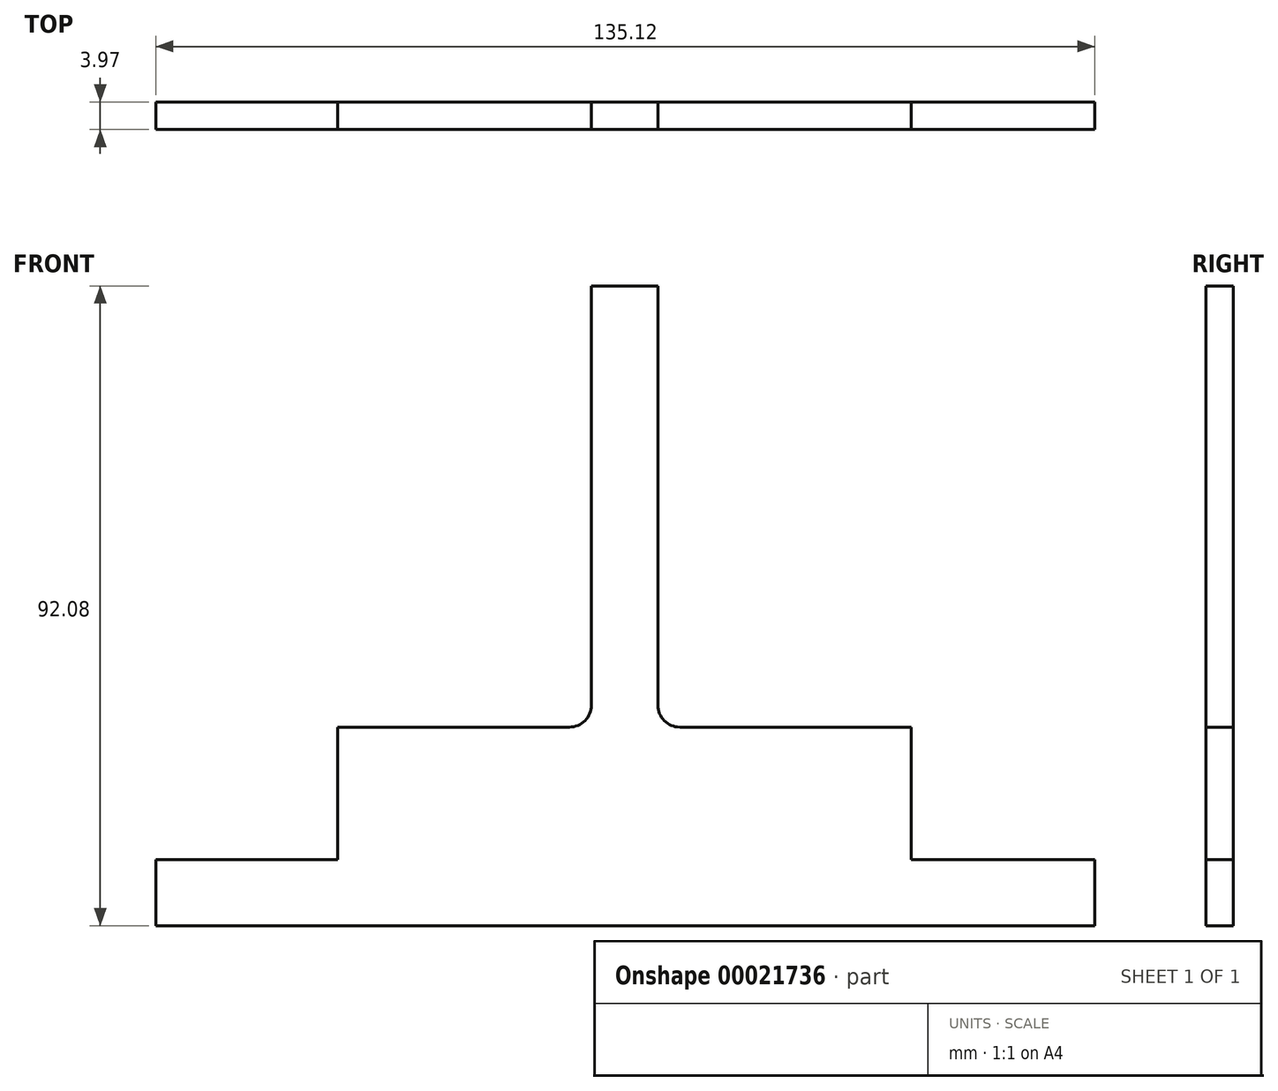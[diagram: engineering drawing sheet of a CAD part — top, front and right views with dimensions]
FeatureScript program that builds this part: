
annotation { "Feature Type Name" : "Feature", "Feature Type Description" : "" }
export const myFeature = defineFeature(function(context is Context, id is Id, definition is map)
    precondition{}
    {
        {
            var Q0;
            Q0=qCreatedBy(makeId("Front.planeOp"),FACE);
            var sketch = newSketch(context, id + "F0", { "sketchPlane" : qUnion([Q0])});
            skLineSegment(sketch, "E0", {"start": v(0, 0) * mm, "end": v(67.56, 0) * mm});
            skLineSegment(sketch, "E1", {"start": v(0, 0) * mm, "end": v(-67.56, 0) * mm});
            skLineSegment(sketch, "E2", {"start": v(-0.1, 92.07) * mm, "end": v(4.67, 92.07) * mm});
            skLineSegment(sketch, "E3", {"start": v(-0.1, 92.07) * mm, "end": v(-4.87, 92.07) * mm});
            skLineSegment(sketch, "E4", {"start": v(-4.87, 92.07) * mm, "end": v(-4.87, 31.75) * mm});
            skLineSegment(sketch, "E5", {"start": v(4.67, 92.07) * mm, "end": v(4.67, 31.75) * mm});
            skPoint(sketch, "E6.visualSharp", {"position": v(4.67, 28.57) * mm});
            skArc(sketch, "E6.filletArc", {"start": v(4.67, 31.75) * mm, "mid": v(5.6, 29.5) * mm, "end": v(7.84, 28.57) * mm});
            skPoint(sketch, "E7.visualSharp", {"position": v(-4.87, 28.57) * mm});
            skArc(sketch, "E7.filletArc", {"start": v(-8.05, 28.57) * mm, "mid": v(-5.8, 29.5) * mm, "end": v(-4.87, 31.75) * mm});
            skLineSegment(sketch, "E8", {"start": v(4.67, 28.57) * mm, "end": v(41.18, 28.58) * mm});
            skLineSegment(sketch, "E9", {"start": v(41.18, 28.58) * mm, "end": v(41.18, 9.53) * mm});
            skLineSegment(sketch, "E10", {"start": v(41.18, 9.53) * mm, "end": v(67.56, 9.53) * mm});
            skLineSegment(sketch, "E11", {"start": v(-4.87, 28.57) * mm, "end": v(-41.38, 28.57) * mm});
            skLineSegment(sketch, "E12", {"start": v(-41.38, 28.57) * mm, "end": v(-41.38, 9.53) * mm});
            skLineSegment(sketch, "E13", {"start": v(-41.38, 9.53) * mm, "end": v(-67.56, 9.53) * mm});
            skLineSegment(sketch, "E14", {"start": v(67.56, 9.53) * mm, "end": v(67.56, 0) * mm});
            skLineSegment(sketch, "E15", {"start": v(-67.56, 9.53) * mm, "end": v(-67.56, 0) * mm});
            skSolve(sketch);
        }
        {
            var Q0;
            Q0=makeQuery(id+"F0.imprint","IMPRINT",FACE,{"disambiguationData":[TD([[makeQuery(id+"F0.imprint","IMPRINT",EDGE,{"derivedFrom":sQuery(id+"F0.wireOp",EDGE,"E0")}),1.0]])]});
            extrude(context, id + "F1", {"entities" : qUnion([Q0]), "depth" : 3.97 * mm});
        }
    });
